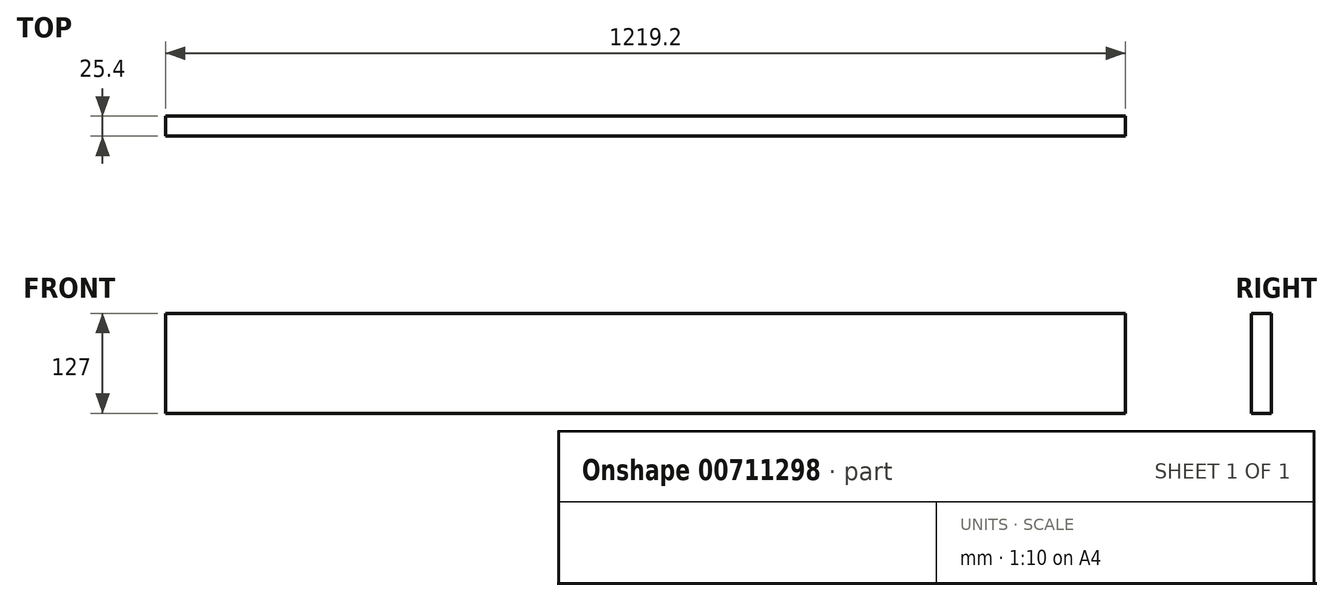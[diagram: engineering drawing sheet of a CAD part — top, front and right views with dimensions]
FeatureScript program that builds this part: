
annotation { "Feature Type Name" : "Feature", "Feature Type Description" : "" }
export const myFeature = defineFeature(function(context is Context, id is Id, definition is map)
    precondition{}
    {
        {
            var Q0;
            Q0=qCreatedBy(makeId("Front.planeOp"),FACE);
            var sketch = newSketch(context, id + "F0", { "sketchPlane" : qUnion([Q0])});
            skLineSegment(sketch, "E0", {"start": v(-558.45, 33.13) * mm, "end": v(660.75, 33.13) * mm});
            skLineSegment(sketch, "E1", {"start": v(-558.45, -93.87) * mm, "end": v(660.75, -93.87) * mm});
            skLineSegment(sketch, "E2", {"start": v(-558.45, 33.13) * mm, "end": v(-558.45, -93.87) * mm});
            skLineSegment(sketch, "E3", {"start": v(660.75, 33.13) * mm, "end": v(660.75, -93.87) * mm});
            skSolve(sketch);
        }
        {
            var Q0;
            Q0 = qSketchRegion(id + "F0", true);
            extrude(context, id + "F1", {"entities" : qUnion([Q0]), "endBound" : BoundingType.SYMMETRIC, "depth" : 25.4 * mm, "offsetDistance" : 25.4 * mm});
        }
    });
